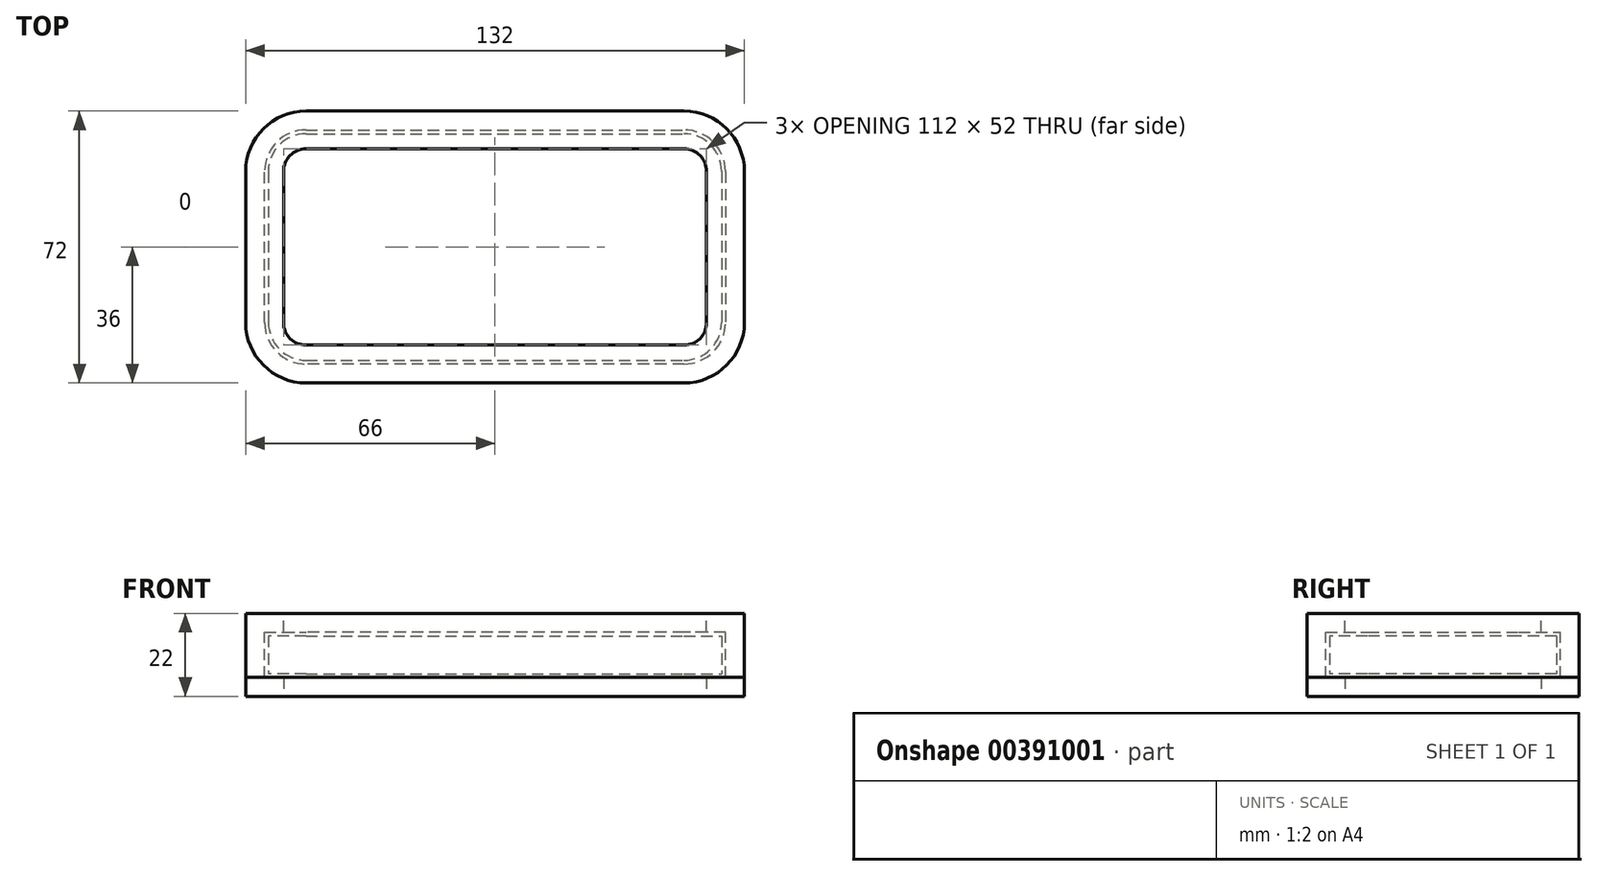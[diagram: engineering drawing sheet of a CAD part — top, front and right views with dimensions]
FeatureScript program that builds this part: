
annotation { "Feature Type Name" : "Feature", "Feature Type Description" : "" }
export const myFeature = defineFeature(function(context is Context, id is Id, definition is map)
    precondition{}
    {
        {
            assignVariable(context, id + "F0", {"name" : "epaisseur_phone", "anyValue" : 10});
        }
        {
            assignVariable(context, id + "F1", {"name" : "epaisseur_coque", "anyValue" : 5});
        }
        {
            var Q0;
            Q0=qCreatedBy(makeId("Top.planeOp"),FACE);
            var sketch = newSketch(context, id + "F2", { "sketchPlane" : qUnion([Q0])});
            skLineSegment(sketch, "E0.bottom", {"start": v(-50, 30) * mm, "end": v(50, 30) * mm});
            skLineSegment(sketch, "E0.top", {"start": v(-50, -30) * mm, "end": v(50, -30) * mm});
            skLineSegment(sketch, "E0.left", {"start": v(-60, 20) * mm, "end": v(-60, -20) * mm});
            skLineSegment(sketch, "E0.right", {"start": v(60, 20) * mm, "end": v(60, -20) * mm});
            skPoint(sketch, "E0.middle", {"position": v(0, 0) * mm});
            skPoint(sketch, "E1.visualSharp", {"position": v(-60, -30) * mm});
            skArc(sketch, "E1.filletArc", {"start": v(-60, -20) * mm, "mid": v(-57.07, -27.07) * mm, "end": v(-50, -30) * mm});
            skPoint(sketch, "E2.visualSharp", {"position": v(-60, 30) * mm});
            skArc(sketch, "E2.filletArc", {"start": v(-50, 30) * mm, "mid": v(-57.07, 27.07) * mm, "end": v(-60, 20) * mm});
            skPoint(sketch, "E3.visualSharp", {"position": v(60, 30) * mm});
            skArc(sketch, "E3.filletArc", {"start": v(60, 20) * mm, "mid": v(57.07, 27.07) * mm, "end": v(50, 30) * mm});
            skPoint(sketch, "E4.visualSharp", {"position": v(60, -30) * mm});
            skArc(sketch, "E4.filletArc", {"start": v(50, -30) * mm, "mid": v(57.07, -27.07) * mm, "end": v(60, -20) * mm});
            skLineSegment(sketch, "E5.0", {"start": v(-61, 20) * mm, "end": v(-61, -20) * mm});
            skArc(sketch, "E5.1", {"start": v(-50, 31) * mm, "mid": v(-57.78, 27.78) * mm, "end": v(-61, 20) * mm});
            skArc(sketch, "E5.2", {"start": v(-61, -20) * mm, "mid": v(-57.78, -27.78) * mm, "end": v(-50, -31) * mm});
            skLineSegment(sketch, "E5.3", {"start": v(-50, 31) * mm, "end": v(0, 31) * mm});
            skLineSegment(sketch, "E5.4", {"start": v(-50, -31) * mm, "end": v(50, -31) * mm});
            skArc(sketch, "E5.5", {"start": v(50, -31) * mm, "mid": v(57.78, -27.78) * mm, "end": v(61, -20) * mm});
            skLineSegment(sketch, "E5.6", {"start": v(61, 20) * mm, "end": v(61, -20) * mm});
            skArc(sketch, "E5.7", {"start": v(61, 20) * mm, "mid": v(57.78, 27.78) * mm, "end": v(50, 31) * mm});
            skLineSegment(sketch, "E6.0", {"start": v(-66, 20) * mm, "end": v(-66, -20) * mm});
            skArc(sketch, "E6.1", {"start": v(-50, 36) * mm, "mid": v(-61.31, 31.31) * mm, "end": v(-66, 20) * mm});
            skArc(sketch, "E6.2", {"start": v(-66, -20) * mm, "mid": v(-61.31, -31.31) * mm, "end": v(-50, -36) * mm});
            skLineSegment(sketch, "E6.3", {"start": v(-50, 36) * mm, "end": v(50, 36) * mm});
            skLineSegment(sketch, "E6.4", {"start": v(-50, -36) * mm, "end": v(50, -36) * mm});
            skArc(sketch, "E6.5", {"start": v(50, -36) * mm, "mid": v(61.31, -31.31) * mm, "end": v(66, -20) * mm});
            skLineSegment(sketch, "E6.6", {"start": v(66, 20) * mm, "end": v(66, -20) * mm});
            skArc(sketch, "E6.7", {"start": v(66, 20) * mm, "mid": v(61.31, 31.31) * mm, "end": v(50, 36) * mm});
            skLineSegment(sketch, "E7", {"start": v(0, 31) * mm, "end": v(50, 31) * mm});
            skSolve(sketch);
        }
        {
            var Q0;
            Q0=makeQuery(id+"F2.imprint","IMPRINT",FACE,{"disambiguationData":[TD([[makeQuery(id+"F2.imprint","IMPRINT",EDGE,{"derivedFrom":sQuery(id+"F2.wireOp",EDGE,"E0.bottom")}),-1.0]])]});
            extrude(context, id + "F3", {"entities" : qUnion([Q0]), "depth" : (getVariable(context, 'epaisseur_phone')) * mm});
        }
        {
            var Q0;
            Q0=qCreatedBy(makeId("Right.planeOp"),FACE);
            var sketch = newSketch(context, id + "F4", { "sketchPlane" : qUnion([Q0])});
            skPoint(sketch, "E8.0", {"position": v(31, 0) * mm});
            skPoint(sketch, "E9.0", {"position": v(36, 0) * mm});
            skPoint(sketch, "E10.0", {"position": v(30, 10) * mm});
            skLineSegment(sketch, "E11", {"start": v(31, -1) * mm, "end": v(31, 11) * mm});
            skLineSegment(sketch, "E12", {"start": v(36, -6) * mm, "end": v(36, 16) * mm});
            skLineSegment(sketch, "E13", {"start": v(26, 11) * mm, "end": v(26, 16) * mm});
            skLineSegment(sketch, "E14", {"start": v(36, 16) * mm, "end": v(26, 16) * mm});
            skLineSegment(sketch, "E15", {"start": v(26, 11) * mm, "end": v(31, 11) * mm});
            skLineSegment(sketch, "E16", {"start": v(36, -6) * mm, "end": v(31, -6) * mm});
            skPoint(sketch, "E17.orphan", {"position": v(31, 16) * mm});
            skLineSegment(sketch, "E18", {"start": v(26, -1) * mm, "end": v(26, -6) * mm});
            skLineSegment(sketch, "E19", {"start": v(26, -6) * mm, "end": v(31, -6) * mm});
            skLineSegment(sketch, "E20", {"start": v(31, -1) * mm, "end": v(26, -1) * mm});
            skSolve(sketch);
        }
        {
            var Q0;
            Q0 = qSketchRegion(id + "F4", true);
            var Q1;
            Q1=sQuery(id+"F2.wireOp",EDGE,"E7");
            var Q2;
            Q2=sQuery(id+"F2.wireOp",EDGE,"E5.7");
            var Q3;
            Q3=sQuery(id+"F2.wireOp",EDGE,"E5.6");
            var Q4;
            Q4=sQuery(id+"F2.wireOp",EDGE,"E5.5");
            var Q5;
            Q5=sQuery(id+"F2.wireOp",EDGE,"E5.4");
            var Q6;
            Q6=sQuery(id+"F2.wireOp",EDGE,"E5.2");
            var Q7;
            Q7=sQuery(id+"F2.wireOp",EDGE,"E5.0");
            var Q8;
            Q8=sQuery(id+"F2.wireOp",EDGE,"E5.1");
            var Q9;
            Q9=sQuery(id+"F2.wireOp",EDGE,"E5.3");
            sweep(context, id + "F5", {"profiles" : qUnion([Q0]), "path" : qUnion([Q1, Q2, Q3, Q4, Q5, Q6, Q7, Q8, Q9])});
        }
        {
            var Q0;
            Q0=makeQuery(id+"F5.opSweep","SWEPT_FACE",FACE,{"disambiguationData":[OSD([sQuery(id+"F2.wireOp",EDGE,"E5.3"),sQuery(id+"F4.wireOp",EDGE,"E16"),sQuery(id+"F4.wireOp",EDGE,"E19")])]});
            var sketch = newSketch(context, id + "F6", { "sketchPlane" : qUnion([Q0])});
            skLineSegment(sketch, "E21.0", {"start": v(-56, -20) * mm, "end": v(-56, 20) * mm});
            skArc(sketch, "E22.0", {"start": v(-50, -26) * mm, "mid": v(-54.24, -24.24) * mm, "end": v(-56, -20) * mm});
            skLineSegment(sketch, "E23.0", {"start": v(50, -26) * mm, "end": v(-50, -26) * mm});
            skArc(sketch, "E24.0", {"start": v(56, -20) * mm, "mid": v(54.24, -24.24) * mm, "end": v(50, -26) * mm});
            skLineSegment(sketch, "E25.0", {"start": v(56, 20) * mm, "end": v(56, -20) * mm});
            skArc(sketch, "E26.0", {"start": v(50, 26) * mm, "mid": v(54.24, 24.24) * mm, "end": v(56, 20) * mm});
            skLineSegment(sketch, "E27.0", {"start": v(-50, 26) * mm, "end": v(50, 26) * mm});
            skArc(sketch, "E28.0", {"start": v(-56, 20) * mm, "mid": v(-54.24, 24.24) * mm, "end": v(-50, 26) * mm});
            skSolve(sketch);
        }
        {
            var Q0;
            Q0=makeQuery(id+"F6.imprint","IMPRINT",FACE,{"disambiguationData":[TD([[makeQuery(id+"F6.imprint","IMPRINT",EDGE,{"derivedFrom":sQuery(id+"F6.wireOp",EDGE,"E21.0")}),-1.0]])]});
            extrude(context, id + "F7", {"entities" : qUnion([Q0]), "oppositeDirection" : true, "depth" : (getVariable(context, 'epaisseur_coque')) * mm});
        }
    });
